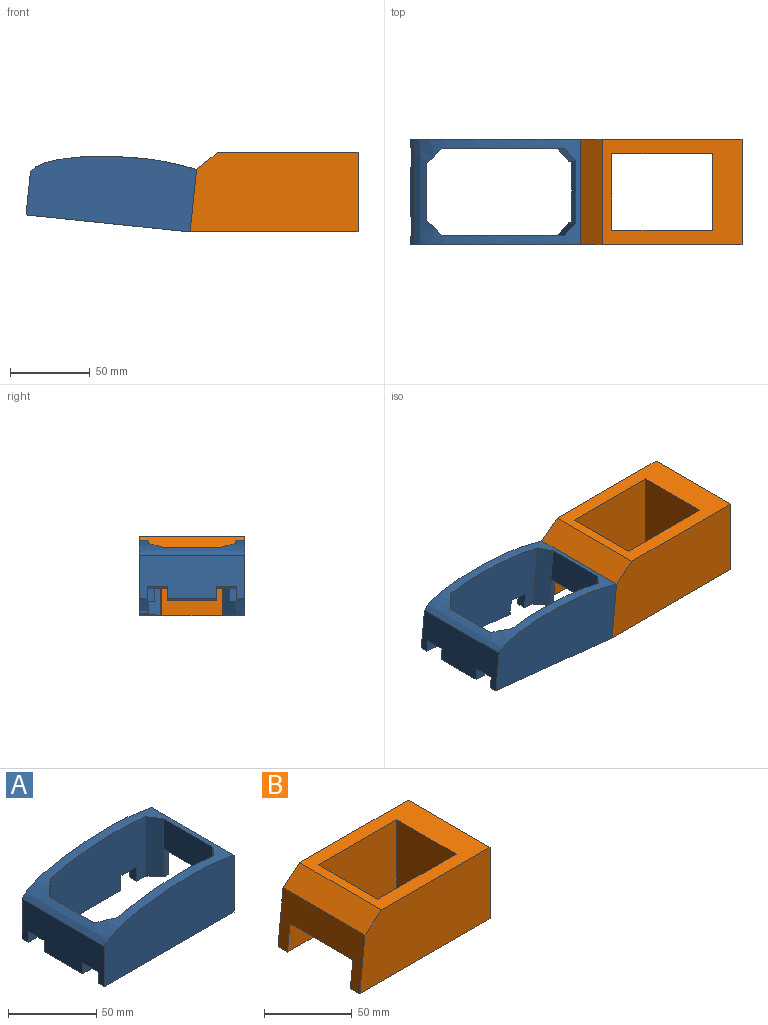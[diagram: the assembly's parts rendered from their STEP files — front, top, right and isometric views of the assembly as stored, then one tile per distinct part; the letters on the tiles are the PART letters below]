
ASSEMBLY  parts=2 mates=1
PART A: 31 faces, bbox 103.5x66.3x45.1 mm
  f0: plane 73.12x9.62mm, normal (0,0,-1), area 433mm2, adj f1,f2,f7,f15,f20,f22,f29
  f1: plane 103.38x45mm, normal (0,1,0), area 3993.1mm2, adj f0,f5,f7,f8,f16,f28,f29,f30
  f2: plane 77.69x43.3mm, normal (0,-1,0), area 3032.2mm2, adj f0,f5,f14,f15,f16,f28,f29,f30
  f3: plane 103.38x14.03mm, normal (0,0,-1), area 668.4mm2, adj f7,f8,f9,f10,f11,f12,f13,f18
  f4: plane 30.88x7.11mm, normal (0,0,-1), area 219.6mm2, adj f6,f7,f21,f25
  f5: plane 17.56x14.03mm, normal (0,0,-1), area 159mm2, adj f1,f2,f8,f13,f14,f19,f28
  f6: plane 36.12x33.04mm, normal (1,0,0), area 1153.4mm2, adj f4,f10,f15,f16,f21,f23,f25,f27
  f7: plane 66.16x27.63mm, normal (-1,0,0), area 1634.7mm2, adj f0,f1,f3,f4,f9,f16,f21,f22
  f8: plane 66.16x39.39mm, normal (1,0,0), area 1880.4mm2, adj f1,f3,f5,f9,f16,f17,f18,f19
  f9: plane 103.38x45mm, normal (0,-1,0), area 4122.1mm2, adj f3,f7,f8,f16
  f10: plane 36.58x9.32mm, normal (0.69,0.72,0), area 394mm2, adj f3,f6,f11,f16,f24,f27
  f11: plane 77.69x43.3mm, normal (0,1,0), area 3161.3mm2, adj f3,f10,f12,f16
  f12: plane 41.16x7.55mm, normal (-0.74,0.68,0), area 410.1mm2, adj f3,f11,f13,f16
  f13: plane 39.97x39.24mm, normal (-1,0,0), area 842.7mm2, adj f3,f5,f12,f14,f16,f17,f18,f19
  f14: plane 41.16x7.55mm, normal (-0.74,-0.68,0), area 410.1mm2, adj f2,f5,f13,f16
  f15: plane 36.58x9.32mm, normal (0.69,-0.72,0), area 394mm2, adj f0,f2,f6,f16,f20,f23
  f16: extruded ~103.38x66.16mm, area 2105.5mm2, adj f1,f2,f6,f7,f8,f9,f10,f11
  f17: plane 38.1x3.47mm, normal (0,0,-1), area 132.1mm2, adj f8,f13,f18,f19
  f18: plane 19.05x3.47mm, normal (0,1,0), area 66.1mm2, adj f3,f8,f13,f17
  f19: plane 19.05x3.47mm, normal (0,-1,0), area 66.1mm2, adj f5,f8,f13,f17
  f20: plane 7.62x4.68mm, normal (-1,0,0), area 35.7mm2, adj f0,f15,f22,f23
  f21: plane 7.62x7.11mm, normal (0,1,0), area 54.2mm2, adj f4,f6,f7,f23
  f22: plane 12.7x7.62mm, normal (0,-1,0), area 96.8mm2, adj f0,f7,f20,f23
  f23: plane 12.7x12.7mm, normal (0,0,-1), area 131.6mm2, adj f6,f7,f15,f20,f21,f22
  f24: plane 7.62x4.68mm, normal (-1,0,0), area 35.7mm2, adj f3,f10,f26,f27
  f25: plane 7.62x7.11mm, normal (0,-1,0), area 54.2mm2, adj f4,f6,f7,f27
  f26: plane 12.7x7.62mm, normal (0,1,0), area 96.8mm2, adj f3,f7,f24,f27
  f27: plane 12.7x12.7mm, normal (0,0,-1), area 131.6mm2, adj f6,f7,f10,f24,f25,f26
  f28: plane 10.16x6.02mm, normal (-1,0,0), area 61.1mm2, adj f1,f2,f5,f30
  f29: plane 10.16x6.02mm, normal (1,0,0), area 61.1mm2, adj f0,f1,f2,f30
  f30: plane 12.7x6.02mm, normal (0,0,-1), area 76.4mm2, adj f1,f2,f28,f29
PART B: 16 faces, bbox 105.2x66.2x50 mm
  f0: plane 87.63x66.16mm, normal (0,0,1), area 2750.4mm2, adj f1,f3,f4,f5,f7,f8,f9,f15
  f1: plane 105.16x50mm, normal (0,-1,0), area 5062.1mm2, adj f0,f2,f6,f8,f15
  f2: plane 66.16x39.18mm, normal (-0.99,0,0.1), area 1633.3mm2, adj f1,f6,f7,f12,f13,f14,f15
  f3: plane 63.27x50mm, normal (0,-1,0), area 3058.5mm2, adj f0,f4,f6,f9,f10,f12
  f4: plane 48.16x30.95mm, normal (1,0,0), area 1490.6mm2, adj f0,f3,f5,f12
  f5: plane 63.27x50mm, normal (0,1,0), area 3058.5mm2, adj f0,f4,f6,f9,f11,f12
  f6: plane 105.16x66.16mm, normal (0,0,-1), area 2700.7mm2, adj f1,f2,f3,f5,f7,f8,f9,f10
  f7: plane 105.16x50mm, normal (0,1,0), area 5062.1mm2, adj f0,f2,f6,f8,f15
  f8: plane 66.16x50mm, normal (1,0,0), area 3308mm2, adj f0,f1,f6,f7
  f9: plane 50x48.16mm, normal (-1,0,0), area 2408mm2, adj f0,f3,f5,f6
  f10: plane 19.05x1.32mm, normal (-1,0,0), area 25.1mm2, adj f3,f6,f12,f13
  f11: plane 19.05x1.32mm, normal (-1,0,0), area 25.1mm2, adj f5,f6,f12,f14
  f12: plane 50.8x27.07mm, normal (0,0,-1), area 1109.7mm2, adj f2,f3,f4,f5,f10,f11,f13,f14
  f13: plane 29.04x19.05mm, normal (0,-1,0), area 534.4mm2, adj f2,f6,f10,f12
  f14: plane 29.04x19.05mm, normal (0,1,0), area 534.4mm2, adj f2,f6,f11,f12
  f15: plane 66.16x13.49mm, normal (-0.63,0,0.78), area 1143.8mm2, adj f0,f1,f2,f7
PLACE A rot(axis=(0,1,0),5.9deg) t=(29.43,-36.82,-18.93)mm
PLACE B t=(133.7,-36.82,-21.62)mm
MATE fastened B.f2 <-> A.f8  axis (-0.99,0,0.1) through (78.54,-69.9,-46.62)mm
